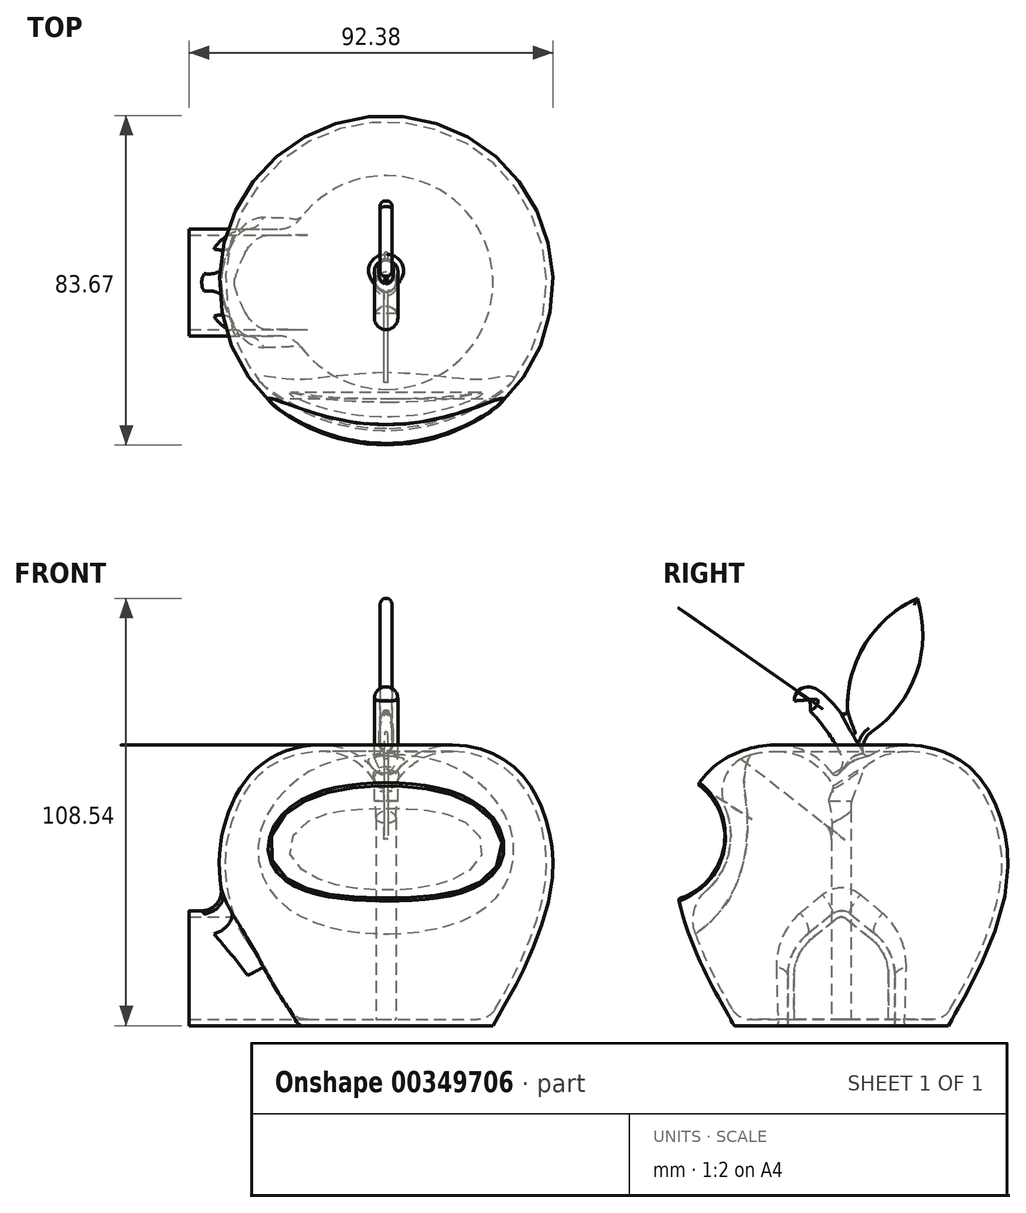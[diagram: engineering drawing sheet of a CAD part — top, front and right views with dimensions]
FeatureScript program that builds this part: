
annotation { "Feature Type Name" : "Feature", "Feature Type Description" : "" }
export const myFeature = defineFeature(function(context is Context, id is Id, definition is map)
    precondition{}
    {
        {
            var Q0;
            Q0=qCreatedBy(makeId("Right.planeOp"),FACE);
            var sketch = newSketch(context, id + "F0", { "sketchPlane" : qUnion([Q0])});
            skLineSegment(sketch, "E0", {"start": v(0, 45.78) * mm, "end": v(0, -10) * mm});
            skFitSpline(sketch, "E1", {"points": [v(0, 45.78) * mm, v(-1.39, 48.7) * mm, v(-10.29, 58.45) * mm, v(-27.9, 56.93) * mm, v(-37.63, 45.78) * mm, v(-40.4, 25.8) * mm, v(-30.98, 0) * mm, v(-26.58, -7.86) * mm, v(-25.26, -9.29) * mm, v(0, -10) * mm], "startDerivative": vector(-75.5, -4.81) * mm, "endDerivative": vector(137.16, 0) * mm});
            skSolve(sketch);
        }
        {
            var Q0;
            Q0=makeQuery(id+"F0.imprint","IMPRINT",FACE,{"disambiguationData":[TD([[makeQuery(id+"F0.imprint","IMPRINT",EDGE,{"derivedFrom":sQuery(id+"F0.wireOp",EDGE,"E0")}),-1.0]])]});
            var Q1;
            Q1=sQuery(id+"F0.wireOp",EDGE,"E0");
            revolve(context, id + "F1", {"entities" : qUnion([Q0]), "axis" : qUnion([Q1]), "revolveType" : RevolveType.FULL});
        }
        {
            var Q0;
            Q0=qCreatedBy(makeId("Top.planeOp"),FACE);
            cPlane(context, id + "F2", {"entities" : qUnion([Q0]), "cplaneType" : CPlaneType.OFFSET, "offset" : 48 * mm, "width" : 152.4 * mm, "height" : 152.4 * mm});
        }
        {
            var Q0;
            Q0=qCreatedBy(makeId("Right.planeOp"),FACE);
            var sketch = newSketch(context, id + "F3", { "sketchPlane" : qUnion([Q0])});
            skCircle(sketch, "E2", {"center": v(-46, 38) * mm, "radius": 18 * mm});
            skSolve(sketch);
        }
        {
            var Q0;
            Q0=qSketchRegion(id+"F3",true);
            extrude(context, id + "F4", {"entities" : qUnion([Q0]), "operationType" : NewBodyOperationType.REMOVE, "depth" : 50.8 * mm, "hasSecondDirection" : true, "secondDirectionOppositeDirection" : true, "secondDirectionDepth" : 50.8 * mm});
        }
        {
            var Q0;
            Q0=qCreatedBy(makeId("Right.planeOp"),FACE);
            var sketch = newSketch(context, id + "F5", { "sketchPlane" : qUnion([Q0])});
            skLineSegment(sketch, "E3.bottom", {"start": v(25, -10) * mm, "end": v(-25, -10) * mm});
            skLineSegment(sketch, "E3.top", {"start": v(25, -20) * mm, "end": v(-25, -20) * mm});
            skLineSegment(sketch, "E3.left", {"start": v(25, -10) * mm, "end": v(25, -20) * mm});
            skLineSegment(sketch, "E3.right", {"start": v(-25, -10) * mm, "end": v(-25, -20) * mm});
            skSolve(sketch);
        }
        {
            var Q0;
            Q0=qSketchRegion(id+"F5",true);
            extrude(context, id + "F6", {"entities" : qUnion([Q0]), "operationType" : NewBodyOperationType.REMOVE, "oppositeDirection" : true, "depth" : 25 * mm, "hasSecondDirection" : true, "secondDirectionOppositeDirection" : false, "secondDirectionDepth" : 25 * mm});
        }
        {
            var Q0;
            Q0=qCreatedBy(makeId("Right.planeOp"),FACE);
            var sketch = newSketch(context, id + "F7", { "sketchPlane" : qUnion([Q0])});
            skArc(sketch, "E4", {"start": v(12, 2.75) * mm, "mid": v(10.83, 7.92) * mm, "end": v(7.54, 12.08) * mm});
            skLineSegment(sketch, "E5", {"start": v(-12, 2.75) * mm, "end": v(-12, -8.4) * mm});
            skLineSegment(sketch, "E6", {"start": v(-12, -8.4) * mm, "end": v(12, -8.4) * mm});
            skLineSegment(sketch, "E7", {"start": v(12, -8.4) * mm, "end": v(12, 2.75) * mm});
            skArc(sketch, "E8", {"start": v(1.26, 17.16) * mm, "mid": v(0, 17.6) * mm, "end": v(-1.26, 17.16) * mm});
            skLineSegment(sketch, "E9", {"start": v(-1.26, 17.16) * mm, "end": v(-7.54, 12.08) * mm});
            skLineSegment(sketch, "E10", {"start": v(1.26, 17.16) * mm, "end": v(7.54, 12.08) * mm});
            skArc(sketch, "E11.trimOffspring", {"start": v(-7.54, 12.08) * mm, "mid": v(-10.83, 7.92) * mm, "end": v(-12, 2.75) * mm});
            skSolve(sketch);
        }
        {
            var Q0;
            Q0=qSketchRegion(id+"F7",true);
            extrude(context, id + "F8", {"entities" : qUnion([Q0]), "operationType" : NewBodyOperationType.ADD, "oppositeDirection" : true, "depth" : 50 * mm});
        }
        {
            var Q0;
            Q0=makeQuery(id+"F6.boolean.opBoolean","COPY",FACE,{"derivedFrom":makeQuery(id+"F6.opExtrude","SWEPT_FACE",FACE,{"disambiguationData":[OSD([sQuery(id+"F5.wireOp",EDGE,"E3.bottom")])]})});
            var Q1;
            Q1=makeQuery(id+"F8.opExtrude","CAP_FACE",FACE,{"disambiguationData":[OSD([sQuery(id+"F7.wireOp",EDGE,"E4")])],"isStart":false});
            shell(context, id + "F9", {"entities" : qUnion([Q0, Q1]), "thickness" : 1.6 * mm, "oppositeDirection" : true});
        }
        {
            var Q0;
            Q0=qCreatedBy(makeId("Right.planeOp"),FACE);
            var sketch = newSketch(context, id + "F10", { "sketchPlane" : qUnion([Q0])});
            skFitSpline(sketch, "E12", {"points": [v(0, 47.1) * mm, v(2.16, 61.38) * mm, v(-9.33, 72.7) * mm], "startDerivative": vector(17.1, 49.07) * mm, "endDerivative": vector(-6.07, -21.24) * mm});
            skSolve(sketch);
        }
        {
            var Q0;
            Q0=qCreatedBy(id+"F2.planeOp",FACE);
            var sketch = newSketch(context, id + "F11", { "sketchPlane" : qUnion([Q0])});
            skCircle(sketch, "E13", {"center": v(0, 0) * mm, "radius": 2.98 * mm});
            skSolve(sketch);
        }
        {
            var Q0;
            Q0=makeQuery(id+"F11.imprint","IMPRINT",FACE,{"disambiguationData":[TD([[makeQuery(id+"F11.imprint","IMPRINT",EDGE,{"derivedFrom":sQuery(id+"F11.wireOp",EDGE,"E13")}),1.0]])]});
            var Q1;
            Q1=sQuery(id+"F10.wireOp",EDGE,"E12");
            sweep(context, id + "F12", {"operationType" : NewBodyOperationType.ADD, "profiles" : qUnion([Q0]), "path" : qUnion([Q1])});
        }
        {
            var Q0;
            Q0=makeQuery(id+"F6.boolean.opBoolean","COPY",FACE,{"derivedFrom":makeQuery(id+"F6.opExtrude","SWEPT_FACE",FACE,{"disambiguationData":[OSD([sQuery(id+"F5.wireOp",EDGE,"E3.bottom")])]})});
            var sketch = newSketch(context, id + "F13", { "sketchPlane" : qUnion([Q0])});
            skCircle(sketch, "E14.0", {"center": v(0, 0) * mm, "radius": 27.15 * mm});
            skSolve(sketch);
        }
        {
            var Q0;
            Q0=qSketchRegion(id+"F13",true);
            extrude(context, id + "F14", {"entities" : qUnion([Q0]), "operationType" : NewBodyOperationType.ADD, "oppositeDirection" : true, "depth" : 1.6 * mm});
        }
        {
            var Q0;
            Q0=makeQuery(id+"F14.opExtrude","CAP_FACE",FACE,{"disambiguationData":[OSD([sQuery(id+"F13.wireOp",EDGE,"E14.0")])],"isStart":false});
            var sketch = newSketch(context, id + "F15", { "sketchPlane" : qUnion([Q0])});
            skCircle(sketch, "E15", {"center": v(0, 0) * mm, "radius": 2.5 * mm});
            skSolve(sketch);
        }
        {
            var Q0;
            Q0=qSketchRegion(id+"F15",true);
            extrude(context, id + "F16", {"entities" : qUnion([Q0]), "operationType" : NewBodyOperationType.ADD, "depth" : 58 * mm});
        }
        {
            var Q0;
            Q0=makeQuery(id+"F16.boolean.opBoolean","INTERSECT",EDGE,{"derivedFrom":[makeQuery(id+"F12.opSweep","CAP_FACE",FACE,{"disambiguationData":[OSD([sQuery(id+"F10.wireOp",VERTEX,"E12.start"),sQuery(id+"F11.wireOp",EDGE,"E13")])],"isStart":true}),makeQuery(id+"F16.opExtrude","SWEPT_FACE",FACE,{"disambiguationData":[OSD([sQuery(id+"F15.wireOp",EDGE,"E15")])]})]});
            fillet(context, id + "F17", {"entities" : qUnion([Q0]), "radius" : 20 * mm, "tangentPropagation" : true, "allowEdgeOverflow" : false});
        }
        {
            var Q0;
            Q0=makeQuery(id+"F16.opExtrude","CAP_EDGE",EDGE,{"disambiguationData":[OSD([sQuery(id+"F15.wireOp",EDGE,"E15")])],"isStart":true});
            var Q1;
            Q1=makeQuery(id+"F14.boolean.opBoolean","INTERSECT",EDGE,{"derivedFrom":[makeQuery(id+"F12.boolean.opBoolean","SPLIT",FACE,{"disambiguationData":[TD([makeQuery(id+"F6.boolean.opBoolean","COPY",FACE,{"derivedFrom":makeQuery(id+"F6.opExtrude","SWEPT_FACE",FACE,{"disambiguationData":[OSD([sQuery(id+"F5.wireOp",EDGE,"E3.bottom")])]})})])],"derivedFrom":makeQuery(id+"F9.opShell","OFFSET_FACE",FACE,{"disambiguationData":[OSD([sQuery(id+"F0.wireOp",EDGE,"E1")]),OD(1.0)]})}),makeQuery(id+"F14.opExtrude","CAP_FACE",FACE,{"disambiguationData":[OSD([sQuery(id+"F13.wireOp",EDGE,"E14.0")])],"isStart":false})]});
            fillet(context, id + "F18", {"entities" : qUnion([Q0, Q1]), "radius" : 5 * mm, "tangentPropagation" : true, "allowEdgeOverflow" : false});
        }
        {
            var Q0;
            Q0=makeQuery(id+"F12.boolean.opBoolean","INTERSECT",EDGE,{"derivedFrom":[makeQuery(id+"F9.opShell","OFFSET_FACE",FACE,{"disambiguationData":[OSD([sQuery(id+"F0.wireOp",EDGE,"E1")]),OD(0.0)]}),makeQuery(id+"F12.opSweep","SWEPT_FACE",FACE,{"disambiguationData":[OSD([sQuery(id+"F10.wireOp",EDGE,"E12"),sQuery(id+"F11.wireOp",EDGE,"E13")])]})]});
            fillet(context, id + "F19", {"entities" : qUnion([Q0]), "radius" : 1 * mm, "tangentPropagation" : true, "allowEdgeOverflow" : false});
        }
        {
            var Q0;
            Q0=qCreatedBy(makeId("Right.planeOp"),FACE);
            var sketch = newSketch(context, id + "F20", { "sketchPlane" : qUnion([Q0])});
            skLineSegment(sketch, "E16", {"start": v(-31.04, -14.45) * mm, "end": v(19.44, 98.92) * mm, "construction": true});
            skPoint(sketch, "E17", {"position": v(-24.6, 0) * mm});
            skLineSegment(sketch, "E18", {"start": v(5.12, 82.95) * mm, "end": v(17.75, 77.33) * mm, "construction": true});
            skArc(sketch, "E19", {"start": v(3, 62) * mm, "mid": v(18.11, 77.16) * mm, "end": v(19.27, 98.54) * mm});
            skArc(sketch, "E20.MirrorCS", {"start": v(3, 62) * mm, "mid": v(4.16, 83.38) * mm, "end": v(19.27, 98.54) * mm});
            skSolve(sketch);
        }
        {
            var Q0;
            Q0=qSketchRegion(id+"F20",true);
            extrude(context, id + "F21", {"entities" : qUnion([Q0]), "operationType" : NewBodyOperationType.ADD, "depth" : 1.5 * mm, "hasSecondDirection" : true, "secondDirectionOppositeDirection" : true, "secondDirectionDepth" : 1.5 * mm});
        }
        {
            var Q0;
            Q0=makeQuery(id+"F9.opShell","OFFSET_EDGE",EDGE,{"disambiguationData":[OSD([sQuery(id+"F0.wireOp",EDGE,"E1"),sQuery(id+"F3.wireOp",EDGE,"E2")])]});
            fillet(context, id + "F22", {"entities" : qUnion([Q0]), "radius" : 10 * mm, "tangentPropagation" : true, "allowEdgeOverflow" : false});
        }
        {
            var Q0;
            {var subQ0=sQuery(id+"F11.wireOp",EDGE,"E13");Q0=makeQuery(id+"F21.boolean.opBoolean","INTERSECT",EDGE,{"derivedFrom":[makeQuery(id+"F12.boolean.opBoolean","SPLIT",FACE,{"disambiguationData":[TD([makeQuery(id+"F1.opRevolve","SWEPT_FACE",FACE,{"disambiguationData":[OSD([sQuery(id+"F0.wireOp",EDGE,"E1")])]})])],"derivedFrom":makeQuery(id+"F12.opSweep","SWEPT_FACE",FACE,{"disambiguationData":[OSD([sQuery(id+"F10.wireOp",EDGE,"E12"),subQ0])]})}),makeQuery(id+"F21.opExtrude","SWEPT_FACE",FACE,{"disambiguationData":[OSD([sQuery(id+"F20.wireOp",EDGE,"E19")])]})]});}
            fillet(context, id + "F23", {"entities" : qUnion([Q0]), "radius" : 5 * mm, "tangentPropagation" : true, "allowEdgeOverflow" : false});
        }
        {
            var Q0;
            Q0=makeQuery(id+"F21.opExtrude","CAP_EDGE",EDGE,{"disambiguationData":[OSD([sQuery(id+"F20.wireOp",EDGE,"E20.MirrorCS")])],"isStart":true});
            var Q1;
            Q1=makeQuery(id+"F21.opExtrude","CAP_EDGE",EDGE,{"disambiguationData":[OSD([sQuery(id+"F20.wireOp",EDGE,"E20.MirrorCS")])],"isStart":false});
            var Q2;
            Q2=makeQuery(id+"F21.opExtrude","CAP_EDGE",EDGE,{"disambiguationData":[OSD([sQuery(id+"F20.wireOp",EDGE,"E19")])],"isStart":true});
            var Q3;
            Q3=makeQuery(id+"F21.opExtrude","CAP_EDGE",EDGE,{"disambiguationData":[OSD([sQuery(id+"F20.wireOp",EDGE,"E19")])],"isStart":false});
            fillet(context, id + "F24", {"entities" : qUnion([Q0, Q1, Q2, Q3]), "radius" : 1.2 * mm, "tangentPropagation" : true, "allowEdgeOverflow" : false});
        }
        {
            var Q0;
            Q0=makeQuery(id+"F4.boolean.opBoolean","INTERSECT",EDGE,{"derivedFrom":[makeQuery(id+"F1.opRevolve","SWEPT_FACE",FACE,{"disambiguationData":[OSD([sQuery(id+"F0.wireOp",EDGE,"E1")])]}),makeQuery(id+"F4.opExtrude","SWEPT_FACE",FACE,{"disambiguationData":[OSD([sQuery(id+"F3.wireOp",EDGE,"E2")])]})]});
            fillet(context, id + "F25", {"entities" : qUnion([Q0]), "radius" : 0.6 * mm, "tangentPropagation" : true, "allowEdgeOverflow" : false});
        }
        {
            var Q0;
            Q0=makeQuery(id+"F8.boolean.opBoolean","INTERSECT",EDGE,{"derivedFrom":[makeQuery(id+"F1.opRevolve","SWEPT_FACE",FACE,{"disambiguationData":[OSD([sQuery(id+"F0.wireOp",EDGE,"E1")])]}),makeQuery(id+"F8.opExtrude","SWEPT_FACE",FACE,{"disambiguationData":[OSD([sQuery(id+"F7.wireOp",EDGE,"E5")])]})]});
            fillet(context, id + "F26", {"entities" : qUnion([Q0]), "radius" : 5 * mm, "tangentPropagation" : true, "allowEdgeOverflow" : false});
        }
        {
            var Q0;
            {var subQ0=sQuery(id+"F11.wireOp",EDGE,"E13");Q0=makeQuery(id+"F24.opFillet","BLEND_EDGE",EDGE,{"blendedFrom":[makeQuery(id+"F21.opExtrude","CAP_EDGE",EDGE,{"disambiguationData":[OSD([sQuery(id+"F20.wireOp",EDGE,"E20.MirrorCS")])],"isStart":true}),makeQuery(id+"F12.boolean.opBoolean","SPLIT",FACE,{"disambiguationData":[TD([makeQuery(id+"F1.opRevolve","SWEPT_FACE",FACE,{"disambiguationData":[OSD([sQuery(id+"F0.wireOp",EDGE,"E1")])]})])],"derivedFrom":makeQuery(id+"F12.opSweep","SWEPT_FACE",FACE,{"disambiguationData":[OSD([sQuery(id+"F10.wireOp",EDGE,"E12"),subQ0])]})})],"blendedInto":[makeQuery(id+"F12.boolean.opBoolean","SPLIT",FACE,{"disambiguationData":[TD([makeQuery(id+"F1.opRevolve","SWEPT_FACE",FACE,{"disambiguationData":[OSD([sQuery(id+"F0.wireOp",EDGE,"E1")])]})])],"derivedFrom":makeQuery(id+"F12.opSweep","SWEPT_FACE",FACE,{"disambiguationData":[OSD([sQuery(id+"F10.wireOp",EDGE,"E12"),subQ0])]})})]});}
            var Q1;
            {var subQ0=sQuery(id+"F11.wireOp",EDGE,"E13");Q1=makeQuery(id+"F24.opFillet","BLEND_EDGE",EDGE,{"blendedFrom":[makeQuery(id+"F21.opExtrude","CAP_EDGE",EDGE,{"disambiguationData":[OSD([sQuery(id+"F20.wireOp",EDGE,"E19")])],"isStart":true}),makeQuery(id+"F12.boolean.opBoolean","SPLIT",FACE,{"disambiguationData":[TD([makeQuery(id+"F1.opRevolve","SWEPT_FACE",FACE,{"disambiguationData":[OSD([sQuery(id+"F0.wireOp",EDGE,"E1")])]})])],"derivedFrom":makeQuery(id+"F12.opSweep","SWEPT_FACE",FACE,{"disambiguationData":[OSD([sQuery(id+"F10.wireOp",EDGE,"E12"),subQ0])]})})],"blendedInto":[makeQuery(id+"F12.boolean.opBoolean","SPLIT",FACE,{"disambiguationData":[TD([makeQuery(id+"F1.opRevolve","SWEPT_FACE",FACE,{"disambiguationData":[OSD([sQuery(id+"F0.wireOp",EDGE,"E1")])]})])],"derivedFrom":makeQuery(id+"F12.opSweep","SWEPT_FACE",FACE,{"disambiguationData":[OSD([sQuery(id+"F10.wireOp",EDGE,"E12"),subQ0])]})})]});}
            fillet(context, id + "F27", {"entities" : qUnion([Q0, Q1]), "radius" : 1 * mm, "tangentPropagation" : true, "allowEdgeOverflow" : false});
        }
        {
            var Q0;
            Q0=makeQuery(id+"F12.boolean.opBoolean","INTERSECT",EDGE,{"derivedFrom":[makeQuery(id+"F1.opRevolve","SWEPT_FACE",FACE,{"disambiguationData":[OSD([sQuery(id+"F0.wireOp",EDGE,"E1")])]}),makeQuery(id+"F12.opSweep","SWEPT_FACE",FACE,{"disambiguationData":[OSD([sQuery(id+"F10.wireOp",EDGE,"E12"),sQuery(id+"F11.wireOp",EDGE,"E13")])]})]});
            fillet(context, id + "F28", {"entities" : qUnion([Q0]), "radius" : 1 * mm, "tangentPropagation" : true, "allowEdgeOverflow" : false});
        }
        {
            var Q0;
            Q0=qCreatedBy(makeId("Right.planeOp"),FACE);
            var sketch = newSketch(context, id + "F29", { "sketchPlane" : qUnion([Q0])});
            skLineSegment(sketch, "E21", {"start": v(-25.98, 58.23) * mm, "end": v(0, 37.93) * mm});
            skLineSegment(sketch, "E22", {"start": v(0, 37.93) * mm, "end": v(0, 52) * mm});
            skLineSegment(sketch, "E23", {"start": v(0, 52) * mm, "end": v(-1.9, 52) * mm});
            skArc(sketch, "E24", {"start": v(-1.9, 52) * mm, "mid": v(-12.68, 60) * mm, "end": v(-25.98, 58.23) * mm});
            skLineSegment(sketch, "E25", {"start": v(0, 72.38) * mm, "end": v(0, 19.91) * mm, "construction": true});
            skSolve(sketch);
        }
        {
            var Q0;
            Q0 = qSketchRegion(id + "F29", true);
            extrude(context, id + "F30", {"entities" : qUnion([Q0]), "operationType" : NewBodyOperationType.ADD, "depth" : 0.5 * mm, "hasSecondDirection" : true, "secondDirectionOppositeDirection" : true, "secondDirectionDepth" : 0.5 * mm});
        }
        {
            var Q0;
            Q0=makeQuery(id+"F30.boolean.opBoolean","INTERSECT",EDGE,{"derivedFrom":[makeQuery(id+"F16.opExtrude","SWEPT_FACE",FACE,{"disambiguationData":[OSD([sQuery(id+"F15.wireOp",EDGE,"E15")])]}),makeQuery(id+"F30.opExtrude","SWEPT_FACE",FACE,{"disambiguationData":[OSD([sQuery(id+"F29.wireOp",EDGE,"E21")])]})]});
            fillet(context, id + "F31", {"entities" : qUnion([Q0]), "radius" : 5 * mm, "tangentPropagation" : true, "allowEdgeOverflow" : false});
        }
    });
